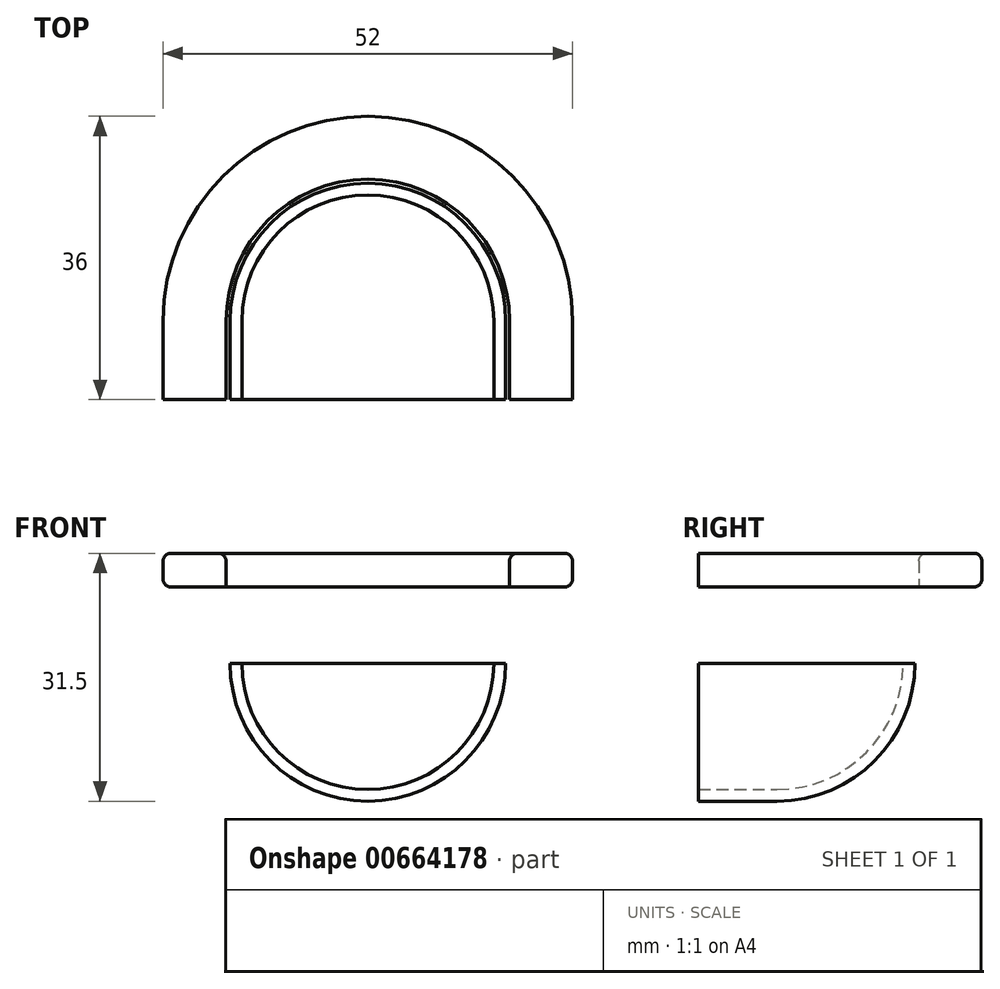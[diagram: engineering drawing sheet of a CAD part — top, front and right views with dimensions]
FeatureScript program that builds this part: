
annotation { "Feature Type Name" : "Feature", "Feature Type Description" : "" }
export const myFeature = defineFeature(function(context is Context, id is Id, definition is map)
    precondition{}
    {
        {
            var Q0;
            Q0=qCreatedBy(makeId("Front.planeOp"),FACE);
            var sketch = newSketch(context, id + "F0", { "sketchPlane" : qUnion([Q0])});
            skLineSegment(sketch, "E0.MirrorCS", {"start": v(17.5, 0) * mm, "end": v(-17.5, 0) * mm});
            skCircle(sketch, "E1", {"center": v(0, 0) * mm, "radius": 17.5 * mm});
            skSolve(sketch);
        }
        {
            var Q0;
            Q0=makeQuery(id+"F0.imprint","IMPRINT",FACE,{"disambiguationData":[TD([[makeQuery(id+"F0.imprint","IMPRINT",EDGE,{"derivedFrom":sQuery(id+"F0.wireOp",EDGE,"LefxOoeR-nq5w-59BA-Ikxv-zXAR8450YXsB.bottom")}),1.0]])]});
            var Q1;
            Q1=makeQuery(id+"F0.imprint","IMPRINT",FACE,{"disambiguationData":[TD([[makeQuery(id+"F0.imprint","IMPRINT",EDGE,{"derivedFrom":sQuery(id+"F0.wireOp",EDGE,"BH197fx9-mUJi-XVLk-NfY7-dZP8ODIYXxIu.bottom")}),-1.0]])]});
            var Q2;
            {var subQ0=sQuery(id+"F0.wireOp",EDGE,"b87kBhWs-2jqE-wdKO-lste-84mNgOiw3cMt.bottom");Q2=makeQuery(id+"F0.imprint","IMPRINT",FACE,{"disambiguationData":[TD([[makeQuery(id+"F0.imprint","IMPRINT",EDGE,{"derivedFrom":subQ0}),1.0]])]});}
            var Q3;
            {var subQ0=sQuery(id+"F0.wireOp",EDGE,"b87kBhWs-2jqE-wdKO-lste-84mNgOiw3cMt.bottom");Q3=makeQuery(id+"F0.imprint","IMPRINT",FACE,{"disambiguationData":[TD([[makeQuery(id+"F0.imprint","IMPRINT",EDGE,{"derivedFrom":subQ0}),-1.0]])]});}
            var Q4;
            Q4=makeQuery(id+"F0.imprint","IMPRINT",FACE,{"disambiguationData":[TD([[makeQuery(id+"F0.imprint","IMPRINT",EDGE,{"derivedFrom":sQuery(id+"F0.wireOp",EDGE,"abc961ae-97f4-4280-a506-1ad7eaece7e70.MirrorCS")}),-1.0]])]});
            var Q5;
            Q5=makeQuery(id+"F0.imprint","IMPRINT",FACE,{"disambiguationData":[TD([[makeQuery(id+"F0.imprint","IMPRINT",EDGE,{"derivedFrom":sQuery(id+"F0.wireOp",EDGE,"b87kBhWs-2jqE-wdKO-lste-84mNgOiw3cMt.top")}),-1.0]])]});
            var Q6;
            Q6=makeQuery(id+"F0.imprint","IMPRINT",FACE,{"disambiguationData":[TD([[makeQuery(id+"F0.imprint","IMPRINT",EDGE,{"derivedFrom":sQuery(id+"F0.wireOp",EDGE,"E0.MirrorCS")}),1.0]])]});
            var Q7;
            Q7=makeQuery(id+"F0.imprint","IMPRINT",FACE,{"disambiguationData":[TD([[makeQuery(id+"F0.imprint","IMPRINT",EDGE,{"derivedFrom":sQuery(id+"F0.wireOp",EDGE,"7HPgpmHj-KFAi-jYJ1-74an-lyGVpWbL82Sj.bottom")}),1.0]])]});
            extrude(context, id + "F1", {"entities" : qUnion([Q0, Q1, Q2, Q3, Q4, Q5, Q6, Q7]), "depth" : 10 * mm, "offsetDistance" : 25 * mm});
        }
        {
            var Q0;
            Q0=qCreatedBy(makeId("Right.planeOp"),FACE);
            var sketch = newSketch(context, id + "F2", { "sketchPlane" : qUnion([Q0])});
            skLineSegment(sketch, "E2", {"start": v(0, 0) * mm, "end": v(17.5, 0) * mm, "construction": true});
            skLineSegment(sketch, "E3", {"start": v(17.5, 0) * mm, "end": v(17.5, 0) * mm});
            skArc(sketch, "E4", {"start": v(0, -17.5) * mm, "mid": v(12.37, -12.37) * mm, "end": v(17.5, 0) * mm});
            skSolve(sketch);
        }
        {
            var Q0;
            Q0=makeQuery(id+"F0.imprint","IMPRINT",FACE,{"disambiguationData":[TD([[makeQuery(id+"F0.imprint","IMPRINT",EDGE,{"derivedFrom":sQuery(id+"F0.wireOp",EDGE,"E0.MirrorCS")}),1.0]])]});
            var Q1;
            Q1=sQuery(id+"F2.wireOp",EDGE,"E4");
            sweep(context, id + "F3", {"operationType" : NewBodyOperationType.ADD, "profiles" : qUnion([Q0]), "path" : qUnion([Q1])});
        }
        {
            var Q0;
            Q0=makeQuery(id+"F1.opExtrude","CAP_FACE",FACE,{"disambiguationData":[OSD([sQuery(id+"F0.wireOp",EDGE,"rlKp1hiw-cRfd-hiZZ-zrK4-8wTFfKo3UoSo"),sQuery(id+"F0.wireOp",EDGE,"b87kBhWs-2jqE-wdKO-lste-84mNgOiw3cMt.top"),sQuery(id+"F0.wireOp",EDGE,"b87kBhWs-2jqE-wdKO-lste-84mNgOiw3cMt.left"),sQuery(id+"F0.wireOp",EDGE,"b87kBhWs-2jqE-wdKO-lste-84mNgOiw3cMt.right"),sQuery(id+"F0.wireOp",EDGE,"LefxOoeR-nq5w-59BA-Ikxv-zXAR8450YXsB.bottom"),sQuery(id+"F0.wireOp",EDGE,"LefxOoeR-nq5w-59BA-Ikxv-zXAR8450YXsB.top"),sQuery(id+"F0.wireOp",EDGE,"LefxOoeR-nq5w-59BA-Ikxv-zXAR8450YXsB.right"),sQuery(id+"F0.wireOp",EDGE,"BH197fx9-mUJi-XVLk-NfY7-dZP8ODIYXxIu.bottom"),sQuery(id+"F0.wireOp",EDGE,"BH197fx9-mUJi-XVLk-NfY7-dZP8ODIYXxIu.top"),sQuery(id+"F0.wireOp",EDGE,"BH197fx9-mUJi-XVLk-NfY7-dZP8ODIYXxIu.right")])],"isStart":false});
            var Q1;
            Q1=makeQuery(id+"F1.opExtrude","SWEPT_FACE",FACE,{"disambiguationData":[OSD([sQuery(id+"F0.wireOp",EDGE,"b87kBhWs-2jqE-wdKO-lste-84mNgOiw3cMt.top"),sQuery(id+"F0.wireOp",EDGE,"LefxOoeR-nq5w-59BA-Ikxv-zXAR8450YXsB.bottom"),sQuery(id+"F0.wireOp",EDGE,"BH197fx9-mUJi-XVLk-NfY7-dZP8ODIYXxIu.bottom")])]});
            var Q2;
            Q2=makeQuery(id+"F1.opExtrude","CAP_FACE",FACE,{"disambiguationData":[OSD([sQuery(id+"F0.wireOp",EDGE,"rlKp1hiw-cRfd-hiZZ-zrK4-8wTFfKo3UoSo"),sQuery(id+"F0.wireOp",EDGE,"b87kBhWs-2jqE-wdKO-lste-84mNgOiw3cMt.top"),sQuery(id+"F0.wireOp",EDGE,"b87kBhWs-2jqE-wdKO-lste-84mNgOiw3cMt.left"),sQuery(id+"F0.wireOp",EDGE,"b87kBhWs-2jqE-wdKO-lste-84mNgOiw3cMt.right"),sQuery(id+"F0.wireOp",EDGE,"LefxOoeR-nq5w-59BA-Ikxv-zXAR8450YXsB.bottom"),sQuery(id+"F0.wireOp",EDGE,"LefxOoeR-nq5w-59BA-Ikxv-zXAR8450YXsB.top"),sQuery(id+"F0.wireOp",EDGE,"LefxOoeR-nq5w-59BA-Ikxv-zXAR8450YXsB.right"),sQuery(id+"F0.wireOp",EDGE,"BH197fx9-mUJi-XVLk-NfY7-dZP8ODIYXxIu.bottom"),sQuery(id+"F0.wireOp",EDGE,"BH197fx9-mUJi-XVLk-NfY7-dZP8ODIYXxIu.top"),sQuery(id+"F0.wireOp",EDGE,"BH197fx9-mUJi-XVLk-NfY7-dZP8ODIYXxIu.right")])],"isStart":true});
            var Q3;
            Q3=makeQuery(id+"F3.opSweep","CAP_FACE",FACE,{"disambiguationData":[OSD([sQuery(id+"F0.wireOp",EDGE,"E0.MirrorCS"),sQuery(id+"F0.wireOp",EDGE,"abc961ae-97f4-4280-a506-1ad7eaece7e76.MirrorCS"),sQuery(id+"F2.wireOp",VERTEX,"E4.end")])],"isStart":false});
            var Q4;
            Q4=makeQuery(id+"F1.opExtrude","CAP_FACE",FACE,{"disambiguationData":[OSD([sQuery(id+"F0.wireOp",EDGE,"E0.MirrorCS"),sQuery(id+"F0.wireOp",EDGE,"abc961ae-97f4-4280-a506-1ad7eaece7e76.MirrorCS")])],"isStart":false});
            var Q5;
            Q5=makeQuery(id+"F1.opExtrude","CAP_FACE",FACE,{"disambiguationData":[OSD([sQuery(id+"F0.wireOp",EDGE,"E1")])],"isStart":false});
            var Q6;
            Q6=makeQuery(id+"F1.opExtrude","CAP_FACE",FACE,{"disambiguationData":[OSD([sQuery(id+"F0.wireOp",EDGE,"E1")])],"isStart":true});
            shell(context, id + "F4", {"entities" : qUnion([Q0, Q1, Q2, Q3, Q4, Q5, Q6]), "thickness" : 1.5 * mm});
        }
        {
            var Q0;
            Q0=makeQuery(id+"F1.opExtrude","CAP_FACE",FACE,{"disambiguationData":[OSD([sQuery(id+"F0.wireOp",EDGE,"E0.MirrorCS"),sQuery(id+"F0.wireOp",EDGE,"abc961ae-97f4-4280-a506-1ad7eaece7e76.MirrorCS")])],"isStart":false});
            var sketch = newSketch(context, id + "F5", { "sketchPlane" : qUnion([Q0])});
            skLineSegment(sketch, "E5.bottom", {"start": v(-16, 0) * mm, "end": v(-26, 0) * mm});
            skLineSegment(sketch, "E5.top", {"start": v(-16, 14) * mm, "end": v(-26, 14) * mm});
            skLineSegment(sketch, "E5.left", {"start": v(-16, 14) * mm, "end": v(-16, 0) * mm});
            skLineSegment(sketch, "E5.right", {"start": v(-26, 14) * mm, "end": v(-26, 0) * mm});
            skLineSegment(sketch, "E6.bottom", {"start": v(-26, 8.3) * mm, "end": v(-18, 8.3) * mm});
            skLineSegment(sketch, "E6.top", {"start": v(-26, 5.7) * mm, "end": v(-18, 5.7) * mm});
            skLineSegment(sketch, "E6.left", {"start": v(-26, 5.7) * mm, "end": v(-26, 8.3) * mm});
            skLineSegment(sketch, "E6.right", {"start": v(-18, 5.7) * mm, "end": v(-18, 8.3) * mm});
            skLineSegment(sketch, "E7.MirrorCS", {"start": v(26, 5.7) * mm, "end": v(18, 5.7) * mm});
            skLineSegment(sketch, "E8.MirrorCS", {"start": v(18, 5.7) * mm, "end": v(18, 8.3) * mm});
            skLineSegment(sketch, "E9.MirrorCS", {"start": v(26, 14) * mm, "end": v(26, 0) * mm});
            skLineSegment(sketch, "E10.MirrorCS", {"start": v(26, 8.3) * mm, "end": v(18, 8.3) * mm});
            skLineSegment(sketch, "E11.MirrorCS", {"start": v(16, 0) * mm, "end": v(26, 0) * mm});
            skLineSegment(sketch, "E12.MirrorCS", {"start": v(26, 5.7) * mm, "end": v(26, 8.3) * mm});
            skLineSegment(sketch, "E13.MirrorCS", {"start": v(16, 14) * mm, "end": v(16, 0) * mm});
            skLineSegment(sketch, "E14.MirrorCS", {"start": v(16, 14) * mm, "end": v(26, 14) * mm});
            skLineSegment(sketch, "E15.bottom", {"start": v(-26, 14) * mm, "end": v(-18, 14) * mm});
            skLineSegment(sketch, "E15.top", {"start": v(-26, 9.7) * mm, "end": v(-18, 9.7) * mm});
            skLineSegment(sketch, "E15.left", {"start": v(-26, 14) * mm, "end": v(-26, 9.7) * mm});
            skLineSegment(sketch, "E15.right", {"start": v(-18, 14) * mm, "end": v(-18, 9.7) * mm});
            skLineSegment(sketch, "E16.bottom", {"start": v(-26, 0) * mm, "end": v(-18, 0) * mm});
            skLineSegment(sketch, "E16.top", {"start": v(-26, 4.3) * mm, "end": v(-18, 4.3) * mm});
            skLineSegment(sketch, "E16.left", {"start": v(-26, 0) * mm, "end": v(-26, 4.3) * mm});
            skLineSegment(sketch, "E16.right", {"start": v(-18, 0) * mm, "end": v(-18, 4.3) * mm});
            skSolve(sketch);
        }
        {
            var Q0;
            {var subQ1=sQuery(id+"F5.wireOp",EDGE,"E5.top");Q0=makeQuery(id+"F5.imprint","IMPRINT",FACE,{"disambiguationData":[TD([[makeQuery(id+"F5.imprint","IMPRINT",EDGE,{"derivedFrom":subQ1}),1.0]])]});}
            var Q1;
            Q1=makeQuery(id+"F3.opSweep","CAP_EDGE",EDGE,{"disambiguationData":[OSD([sQuery(id+"F0.wireOp",EDGE,"abc961ae-97f4-4280-a506-1ad7eaece7e76.MirrorCS"),sQuery(id+"F2.wireOp",VERTEX,"E4.end")])],"isStart":false});
            var Q2;
            {var subQ0=sQuery(id+"F0.wireOp",EDGE,"abc961ae-97f4-4280-a506-1ad7eaece7e76.MirrorCS");var subQ1=sQuery(id+"F0.wireOp",EDGE,"E0.MirrorCS");Q2=makeQuery(id+"F1.opExtrude","SWEPT_EDGE",EDGE,{"disambiguationData":[OSD([subQ1,subQ0]),TDD([makeQuery(id+"F0.imprint","INTERSECT",VERTEX,{"disambiguationData":[OD(1.0)],"derivedFrom":[subQ1,subQ0]})])]});}
            var Q3;
            {var subQ0=sQuery(id+"F0.wireOp",EDGE,"E1");var subQ1=sQuery(id+"F0.wireOp",EDGE,"E0.MirrorCS");Q3=makeQuery(id+"F1.opExtrude","SWEPT_EDGE",EDGE,{"disambiguationData":[OSD([subQ1,subQ0]),TDD([makeQuery(id+"F0.imprint","INTERSECT",VERTEX,{"disambiguationData":[OD(0.0)],"derivedFrom":[subQ1,subQ0]})])]});}
            sweep(context, id + "F6", {"operationType" : NewBodyOperationType.ADD, "profiles" : qUnion([Q0]), "path" : qUnion([Q1, Q2, Q3])});
        }
        {
            var Q0;
            {var subQ0=sQuery(id+"F5.wireOp",EDGE,"E5.left");var subQ1=sQuery(id+"F5.wireOp",EDGE,"E5.top");var subQ2=sQuery(id+"F0.wireOp",EDGE,"E1");var subQ3=sQuery(id+"F0.wireOp",EDGE,"E0.MirrorCS");Q0=makeQuery(id+"F6.opSweep","SWEPT_EDGE",EDGE,{"disambiguationData":[OSD([subQ3,subQ2,subQ1,subQ0]),TDD([makeQuery(id+"F1.opExtrude","SWEPT_EDGE",EDGE,{"disambiguationData":[OSD([subQ3,subQ2]),TDD([makeQuery(id+"F0.imprint","INTERSECT",VERTEX,{"disambiguationData":[OD(0.0)],"derivedFrom":[subQ3,subQ2]})])]}),makeQuery(id+"F5.imprint","INTERSECT",VERTEX,{"derivedFrom":[subQ1,subQ0]})])]});}
            var Q1;
            {var subQ0=sQuery(id+"F5.wireOp",EDGE,"E5.right");var subQ1=sQuery(id+"F5.wireOp",EDGE,"E5.top");var subQ2=sQuery(id+"F0.wireOp",EDGE,"E1");var subQ3=sQuery(id+"F0.wireOp",EDGE,"E0.MirrorCS");Q1=makeQuery(id+"F6.opSweep","SWEPT_EDGE",EDGE,{"disambiguationData":[OSD([subQ3,subQ2,subQ1,subQ0]),TDD([makeQuery(id+"F1.opExtrude","SWEPT_EDGE",EDGE,{"disambiguationData":[OSD([subQ3,subQ2]),TDD([makeQuery(id+"F0.imprint","INTERSECT",VERTEX,{"disambiguationData":[OD(0.0)],"derivedFrom":[subQ3,subQ2]})])]}),makeQuery(id+"F5.imprint","INTERSECT",VERTEX,{"derivedFrom":[subQ1,subQ0]})])]});}
            var Q2;
            {var subQ0=sQuery(id+"F5.wireOp",EDGE,"E5.right");var subQ1=sQuery(id+"F5.wireOp",EDGE,"E5.bottom");var subQ2=sQuery(id+"F0.wireOp",EDGE,"E1");var subQ3=sQuery(id+"F0.wireOp",EDGE,"E0.MirrorCS");Q2=makeQuery(id+"F6.opSweep","SWEPT_EDGE",EDGE,{"disambiguationData":[OSD([subQ3,subQ2,subQ1,subQ0]),TDD([makeQuery(id+"F1.opExtrude","SWEPT_EDGE",EDGE,{"disambiguationData":[OSD([subQ3,subQ2]),TDD([makeQuery(id+"F0.imprint","INTERSECT",VERTEX,{"disambiguationData":[OD(0.0)],"derivedFrom":[subQ3,subQ2]})])]}),makeQuery(id+"F5.imprint","INTERSECT",VERTEX,{"derivedFrom":[subQ1,subQ0]})])]});}
            var Q3;
            Q3=makeQuery(id+"F6.opSweep","SWEPT_EDGE",EDGE,{"disambiguationData":[OSD([sQuery(id+"F0.wireOp",EDGE,"E1"),sQuery(id+"F2.wireOp",VERTEX,"E4.end"),sQuery(id+"F5.wireOp",EDGE,"E5.top"),sQuery(id+"F5.wireOp",EDGE,"E15.bottom"),sQuery(id+"F5.wireOp",EDGE,"E15.right")])]});
            var Q4;
            {var subQ0=sQuery(id+"F5.wireOp",EDGE,"E15.left");var subQ1=sQuery(id+"F5.wireOp",EDGE,"E15.top");var subQ2=sQuery(id+"F5.wireOp",EDGE,"E5.right");var subQ3=sQuery(id+"F0.wireOp",EDGE,"E1");var subQ4=sQuery(id+"F0.wireOp",EDGE,"E0.MirrorCS");Q4=makeQuery(id+"F6.opSweep","SWEPT_EDGE",EDGE,{"disambiguationData":[OSD([subQ4,subQ3,subQ2,subQ1,subQ0]),TDD([makeQuery(id+"F1.opExtrude","SWEPT_EDGE",EDGE,{"disambiguationData":[OSD([subQ4,subQ3]),TDD([makeQuery(id+"F0.imprint","INTERSECT",VERTEX,{"disambiguationData":[OD(1.0)],"derivedFrom":[subQ4,subQ3]})])]}),makeQuery(id+"F5.imprint","INTERSECT",VERTEX,{"derivedFrom":[subQ2,subQ1,subQ0]})])]});}
            var Q5;
            {var subQ0=sQuery(id+"F5.wireOp",EDGE,"E16.left");var subQ1=sQuery(id+"F5.wireOp",EDGE,"E16.top");var subQ2=sQuery(id+"F5.wireOp",EDGE,"E5.right");var subQ3=sQuery(id+"F0.wireOp",EDGE,"E1");var subQ4=sQuery(id+"F0.wireOp",EDGE,"E0.MirrorCS");Q5=makeQuery(id+"F6.opSweep","SWEPT_EDGE",EDGE,{"disambiguationData":[OSD([subQ4,subQ3,subQ2,subQ1,subQ0]),TDD([makeQuery(id+"F1.opExtrude","SWEPT_EDGE",EDGE,{"disambiguationData":[OSD([subQ4,subQ3]),TDD([makeQuery(id+"F0.imprint","INTERSECT",VERTEX,{"disambiguationData":[OD(1.0)],"derivedFrom":[subQ4,subQ3]})])]}),makeQuery(id+"F5.imprint","INTERSECT",VERTEX,{"derivedFrom":[subQ2,subQ1,subQ0]})])]});}
            fillet(context, id + "F7", {"entities" : qUnion([Q0, Q1, Q2, Q3, Q4, Q5]), "radius" : 1 * mm, "tangentPropagation" : true, "allowEdgeOverflow" : false});
        }
    });
